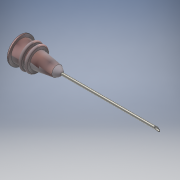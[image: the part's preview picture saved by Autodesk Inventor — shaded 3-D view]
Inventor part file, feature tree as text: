
AUTODESK INVENTOR PART (.ipt)
format: ipt  version: 2018 (Build 220112000, 112)  size: 219,648 bytes
history: native  units: mm
features: sketch x7, extrude x5, revolve x1, plane x1, loft x1, other x1
ambient origin geometry x8: Origin, YZ Plane, XZ Plane, XY Plane, X Axis, Y Axis, Z Axis, Center Point
bodies: Solid1 (feature_tree)
feature tree (16):
  revolve  "Revolution1"  [1 undecoded]
  plane  "Work Plane1"
  loft  "Loft1"
  extrude  "Extrusion1"  Depth=0.75mm
  extrude  "Extrusion2"  Depth=0.5mm
  extrude  "Extrusion3"  Depth=1.0mm
  extrude  "Extrusion4"  Depth=1.0mm
  extrude  "Extrusion5"  Depth=10.0mm
  sketch  "Sketch1"  dims[d3=13.5mm d4=4.0mm]
  sketch  "Sketch2"  dims[d5=2.0mm d6=1.0mm]
  other  "Edges1"
  sketch  "Sketch3"  dims[d7=0.1309mm d11=0.75mm d13=0.75mm]
  sketch  "Sketch4"  dims[d14=1.0mm d15=0.5mm]
  sketch  "Sketch5"  dims[d16=7.3mm d17=1.0mm]
  sketch  "Sketch6"  dims[d20=1.0mm d21=1.0mm]
  sketch  "Sketch7"  dims[d24=1.0mm d25=1.0mm d26=5.0mm d27=90.0deg d28=14.5mm d29=4.0mm d30=0.0mm d31=90.0deg d32=10.0mm d33=90.0deg d34=1.0mm d35=3.0mm d36=0.0mm d37=40.0mm d38=0.0mm d40=7.0mm d41=2.0mm d42=0.0mm d43=0.9mm d44=40.0mm d45=0.0mm d46=2.0mm d47=5.0mm d48=2.0mm d49=0.0mm]
note: 1 required parameter value undecoded (feature->parameter linkage not recoverable at this tier; creation-order binding heuristic only, values carry confidence <= 0.55)
